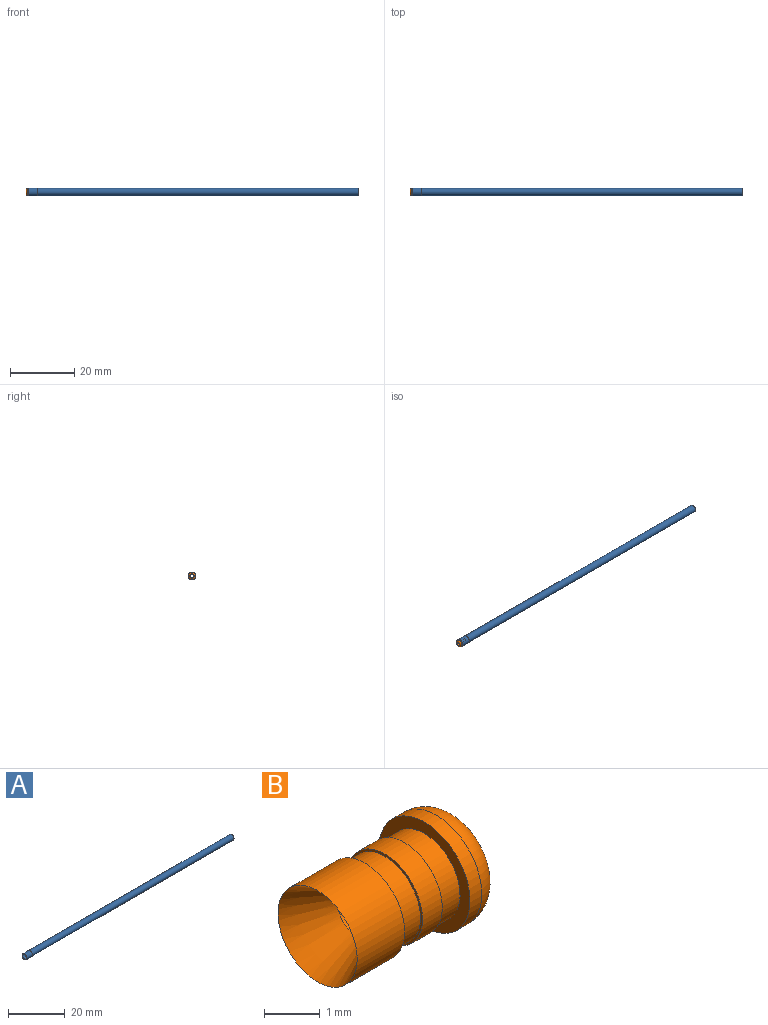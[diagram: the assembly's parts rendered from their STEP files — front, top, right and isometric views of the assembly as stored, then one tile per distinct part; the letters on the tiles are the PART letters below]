
ASSEMBLY  parts=2 mates=1
PART A: 8 faces, bbox 102.8x2.4x2.4 mm
  f0: cone r=1.22mm half-angle=65.9deg, axis (-1,0,0), area 0.6mm2, adj f1,f7
  f1: cylinder r=1.22mm len=2.8mm, axis (-1,0,0), area 21.5mm2, adj f0,f2
  f2: plane 2.44x2.44mm, normal (-1,0,0), area 1.7mm2, adj f1,f3
  f3: cylinder r=0.97mm len=2.77mm, axis (-1,0,0), area 16.9mm2, adj f2,f4
  f4: cone r=0.9mm half-angle=48.4deg, axis (-1,0,0), area 0.5mm2, adj f3,f5
  f5: cylinder r=0.9mm len=100mm, axis (-1,0,0), area 565.5mm2, adj f4,f6
  f6: plane 2.3x2.3mm, normal (1,0,0), area 1.6mm2, adj f5,f7
  f7: cylinder r=1.15mm len=100mm, axis (-1,0,0), area 722.6mm2, adj f0,f6
PART B: 13 faces, bbox 3.5x2.5x2.5 mm
  f0: cylinder r=1.15mm len=2.3mm, axis (-1,0,0), area 2.2mm2, adj f1,f12
  f1: plane 2.3x2.3mm, normal (-1,0,0), area 1.6mm2, adj f0,f2
  f2: cylinder r=0.9mm len=1.8mm, axis (-1,0,0), area 2.8mm2, adj f1,f3
  f3: plane 1.9x1.9mm, normal (1,0,0), area 0.3mm2, adj f2,f4
  f4: cylinder r=0.95mm len=1.9mm, axis (-1,0,0), area 3mm2, adj f3,f5
  f5: plane 1.9x1.9mm, normal (-1,0,0), area 0.3mm2, adj f4,f6
  f6: cylinder r=0.9mm len=1.8mm, axis (-1,0,0), area 2.8mm2, adj f5,f7
  f7: plane 2x2mm, normal (1,0,0), area 0.6mm2, adj f6,f8
  f8: cylinder r=1mm len=2mm, axis (-1,0,0), area 7.5mm2, adj f7,f9
  f9: cone r=1mm half-angle=26.6deg, axis (-1,0,0), area 5.3mm2, adj f8,f10
  f10: cylinder r=0.5mm len=2.5mm, axis (-1,0,0), area 7.9mm2, adj f9,f11
  f11: plane 1.3x1.3mm, normal (1,0,0), area 0.5mm2, adj f10,f12
  f12: torus R=0.65mm, axis (-1,0,0), area 4.8mm2, adj f0,f11
PLACE A t=(-32.9,4.93,-3.5)mm
PLACE B rot(axis=(0,0,1),180deg) t=(-39.38,4.93,-3.5)mm
MATE cylindrical B.f0 <-> A.f0  axis (1,0,0) through (-38.65,4.93,-3.5)mm
